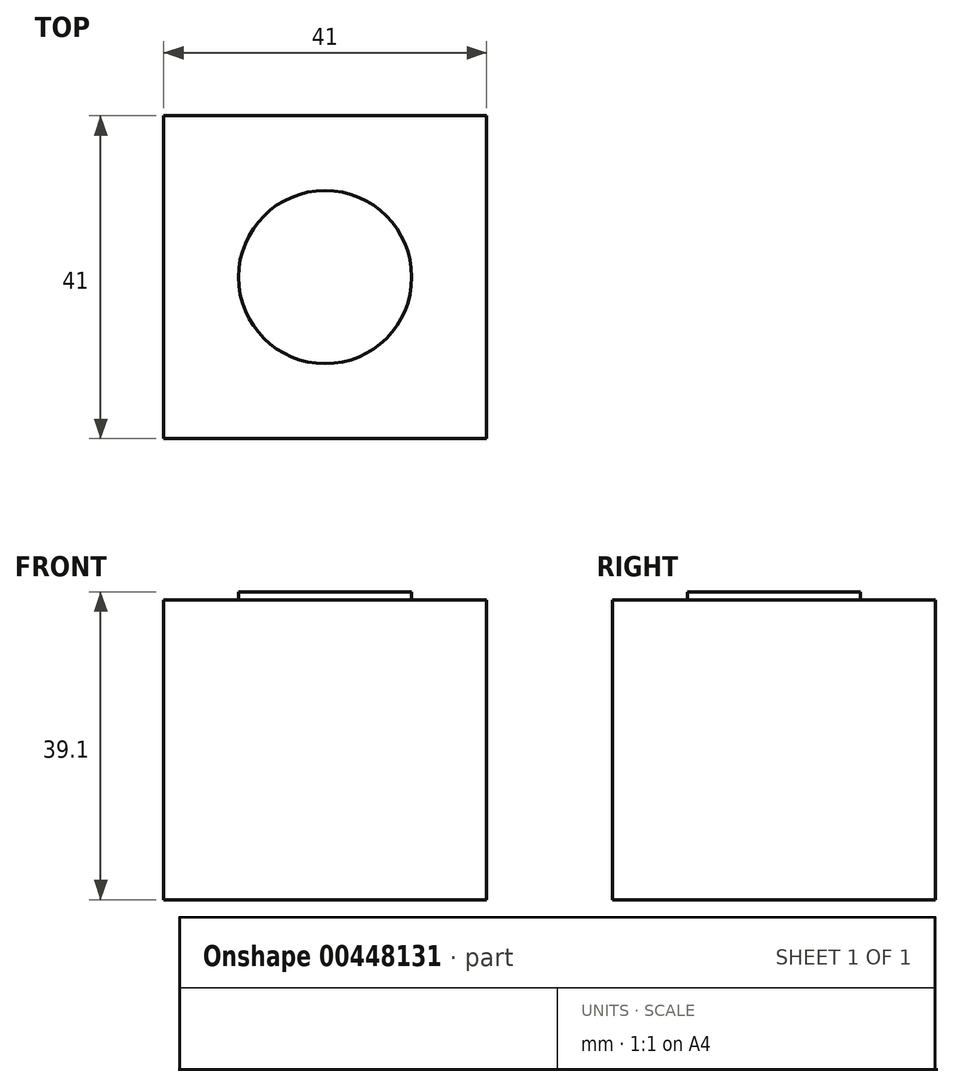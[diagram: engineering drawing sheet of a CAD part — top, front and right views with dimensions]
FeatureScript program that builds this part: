
annotation { "Feature Type Name" : "Feature", "Feature Type Description" : "" }
export const myFeature = defineFeature(function(context is Context, id is Id, definition is map)
    precondition{}
    {
        {
            var Q0;
            Q0=qCreatedBy(makeId("Top.planeOp"),FACE);
            var sketch = newSketch(context, id + "F0", { "sketchPlane" : qUnion([Q0])});
            skLineSegment(sketch, "E0.bottom", {"start": v(20.5, -20.5) * mm, "end": v(-20.5, -20.5) * mm});
            skLineSegment(sketch, "E0.top", {"start": v(20.5, 20.5) * mm, "end": v(-20.5, 20.5) * mm});
            skLineSegment(sketch, "E0.left", {"start": v(20.5, -20.5) * mm, "end": v(20.5, 20.5) * mm});
            skLineSegment(sketch, "E0.right", {"start": v(-20.5, -20.5) * mm, "end": v(-20.5, 20.5) * mm});
            skPoint(sketch, "E0.middle", {"position": v(0, 0) * mm});
            skSolve(sketch);
        }
        {
            var Q0;
            Q0=makeQuery(id+"F0.imprint","IMPRINT",FACE,{"disambiguationData":[TD([[makeQuery(id+"F0.imprint","IMPRINT",EDGE,{"derivedFrom":sQuery(id+"F0.wireOp",EDGE,"E0.bottom")}),-1.0]])]});
            extrude(context, id + "F1", {"entities" : qUnion([Q0]), "flatOperationType" : FlatOperationType.REMOVE, "offsetDistance" : 25.4 * mm, "depth" : 38.1 * mm, "domain" : OperationDomain.MODEL});
        }
        {
            var Q0;
            Q0=makeQuery(id+"F1.opExtrude","CAP_FACE",FACE,{"disambiguationData":[OSD([sQuery(id+"F0.wireOp",EDGE,"E0.bottom"),sQuery(id+"F0.wireOp",EDGE,"E0.top"),sQuery(id+"F0.wireOp",EDGE,"E0.left"),sQuery(id+"F0.wireOp",EDGE,"E0.right")])],"isStart":false});
            var sketch = newSketch(context, id + "F2", { "sketchPlane" : qUnion([Q0])});
            skCircle(sketch, "E1", {"center": v(0, 0) * mm, "radius": 11 * mm});
            skSolve(sketch);
        }
        {
            var Q0;
            Q0 = qSketchRegion(id + "F2", true);
            extrude(context, id + "F3", {"entities" : qUnion([Q0]), "operationType" : NewBodyOperationType.ADD, "depth" : 1 * mm});
        }
        {
            var Q0;
            Q0=makeQuery(id+"F3.opExtrude","CAP_FACE",FACE,{"disambiguationData":[OSD([sQuery(id+"F2.wireOp",EDGE,"E1")])],"isStart":false});
            var sketch = newSketch(context, id + "F4", { "sketchPlane" : qUnion([Q0])});
            skCircle(sketch, "E2", {"center": v(0, 0) * mm, "radius": 2.5 * mm});
            skSolve(sketch);
        }
        {
            var Q0;
            Q0=sQuery(id+"F4.wireOp",EDGE,"E2");
            extrude(context, id + "F5", {"bodyType" : ToolBodyType.SURFACE, "surfaceEntities" : qUnion([Q0]), "depth" : 10 * mm});
        }
    });
